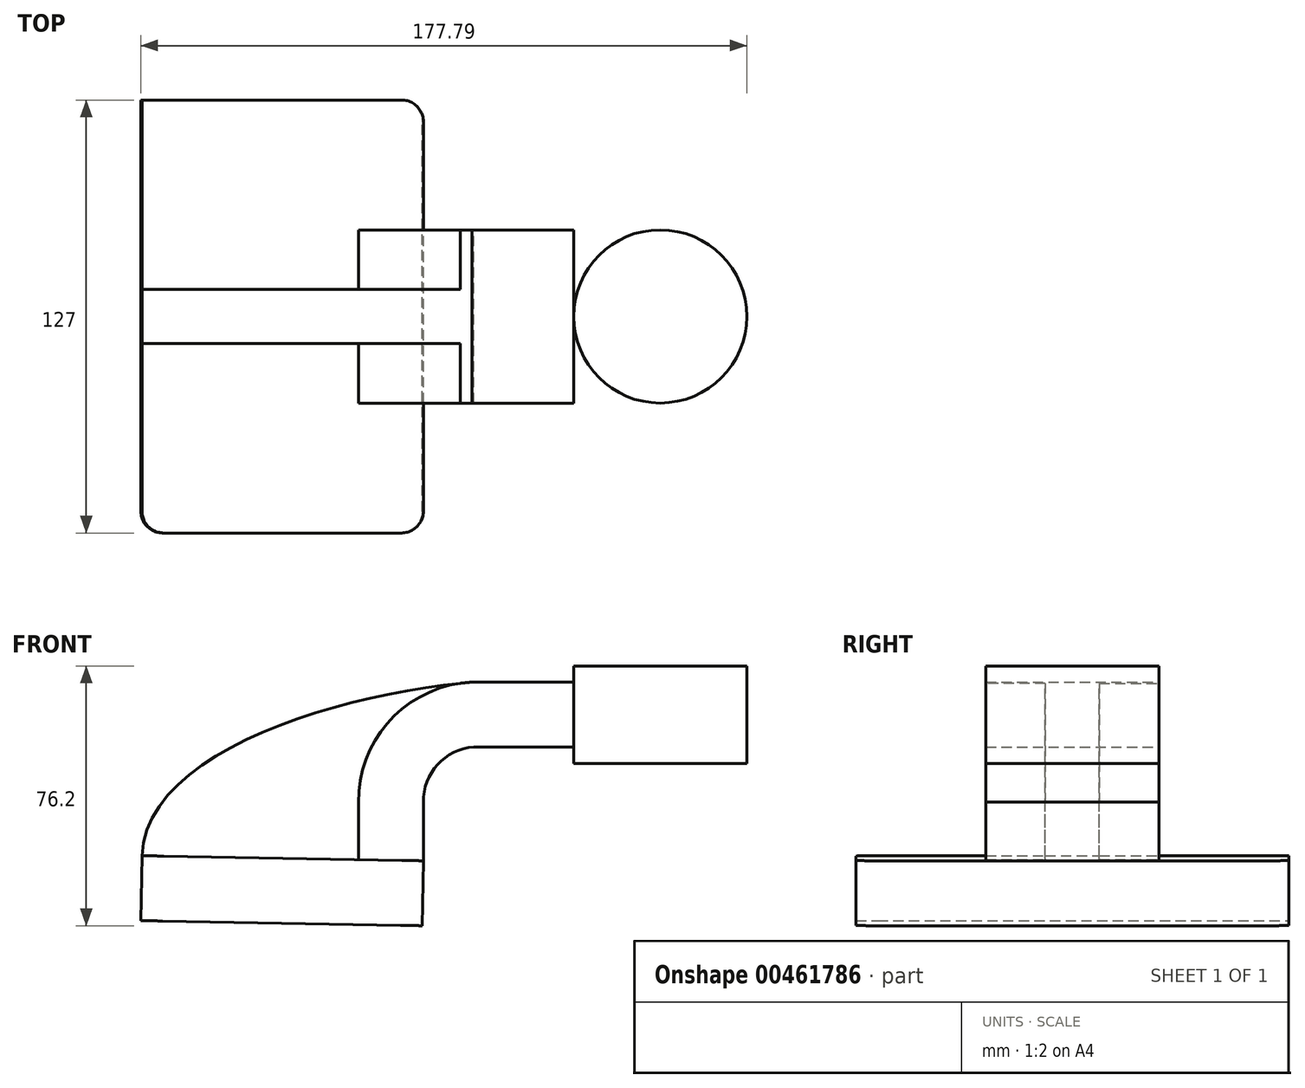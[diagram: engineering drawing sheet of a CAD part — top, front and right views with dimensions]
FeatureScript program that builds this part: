
annotation { "Feature Type Name" : "Feature", "Feature Type Description" : "" }
export const myFeature = defineFeature(function(context is Context, id is Id, definition is map)
    precondition{}
    {
        {
            var Q0;
            Q0=qCreatedBy(makeId("Front.planeOp"),FACE);
            var sketch = newSketch(context, id + "F0", { "sketchPlane" : qUnion([Q0])});
            skLineSegment(sketch, "E0.bottom", {"start": v(41.1, -10.27) * mm, "end": v(-41.44, -8.77) * mm});
            skLineSegment(sketch, "E0.top", {"start": v(41.44, 8.77) * mm, "end": v(-41.1, 10.27) * mm});
            skLineSegment(sketch, "E0.left", {"start": v(41.1, -10.27) * mm, "end": v(41.44, 8.77) * mm});
            skLineSegment(sketch, "E0.right", {"start": v(-41.44, -8.77) * mm, "end": v(-41.1, 10.27) * mm});
            skPoint(sketch, "E0.middle", {"position": v(0, 0) * mm});
            skLineSegment(sketch, "E1", {"start": v(41.44, 8.77) * mm, "end": v(41.45, 26.02) * mm});
            skLineSegment(sketch, "E2.bottom", {"start": v(110.95, 37.35) * mm, "end": v(60.15, 37.35) * mm});
            skLineSegment(sketch, "E2.top", {"start": v(110.95, 65.93) * mm, "end": v(60.15, 65.93) * mm});
            skLineSegment(sketch, "E2.left", {"start": v(110.95, 37.35) * mm, "end": v(110.95, 65.93) * mm});
            skLineSegment(sketch, "E2.right", {"start": v(60.15, 37.35) * mm, "end": v(60.15, 65.93) * mm});
            skPoint(sketch, "E2.middle", {"position": v(85.55, 51.64) * mm});
            skArc(sketch, "E3", {"start": v(56.2, 42.13) * mm, "mid": v(45.62, 37) * mm, "end": v(41.45, 26.02) * mm});
            skLineSegment(sketch, "E4", {"start": v(56.2, 42.13) * mm, "end": v(85.55, 42.13) * mm});
            skLineSegment(sketch, "E5.0", {"start": v(55.64, 61.18) * mm, "end": v(85.55, 61.18) * mm});
            skArc(sketch, "E5.1", {"start": v(55.64, 61.18) * mm, "mid": v(31.9, 50.24) * mm, "end": v(22.4, 25.9) * mm});
            skLineSegment(sketch, "E5.2", {"start": v(22.4, 9.37) * mm, "end": v(22.4, 25.9) * mm});
            skLineSegment(sketch, "E6", {"start": v(85.55, 65.93) * mm, "end": v(85.55, 37.35) * mm});
            skFitSpline(sketch, "E7", {"points": [v(-41.1, 10.27) * mm, v(55.64, 61.18) * mm], "startDerivative": vector(3.4, 93.06) * mm, "endDerivative": vector(113.48, 10) * mm});
            skLineSegment(sketch, "E8", {"start": v(22.4, 9.37) * mm, "end": v(22.4, 9.12) * mm});
            skSolve(sketch);
        }
        {
            var Q0;
            Q0=makeQuery(id+"F0.imprint","IMPRINT",FACE,{"disambiguationData":[TD([[makeQuery(id+"F0.imprint","IMPRINT",EDGE,{"derivedFrom":sQuery(id+"F0.wireOp",EDGE,"E0.bottom")}),-1.0]])]});
            extrude(context, id + "F1", {"entities" : qUnion([Q0]), "endBound" : BoundingType.SYMMETRIC, "depth" : 127 * mm});
        }
        {
            var Q0;
            {var subQ0=sQuery(id+"F0.wireOp",EDGE,"E4");var subQ1=sQuery(id+"F0.wireOp",EDGE,"E2.right");var subQ2=makeQuery(id+"F0.imprint","INTERSECT",VERTEX,{"derivedFrom":[subQ1,subQ0]});Q0=makeQuery(id+"F0.imprint","IMPRINT",FACE,{"disambiguationData":[TD([[makeQuery(id+"F0.imprint","IMPRINT",EDGE,{"disambiguationData":[TD([[subQ2,-1.0]])],"derivedFrom":subQ1}),-1.0]])]});}
            var Q1;
            {var subQ6=sQuery(id+"F0.wireOp",EDGE,"E1");Q1=makeQuery(id+"F0.imprint","IMPRINT",FACE,{"disambiguationData":[TD([[makeQuery(id+"F0.imprint","IMPRINT",EDGE,{"derivedFrom":subQ6}),1.0]])]});}
            extrude(context, id + "F2", {"entities" : qUnion([Q0, Q1]), "operationType" : NewBodyOperationType.ADD, "endBound" : BoundingType.SYMMETRIC, "depth" : 50.8 * mm});
        }
        {
            var Q0;
            {var subQ0=sQuery(id+"F0.wireOp",EDGE,"E5.2");Q0=makeQuery(id+"F0.imprint","IMPRINT",FACE,{"disambiguationData":[TD([[makeQuery(id+"F0.imprint","IMPRINT",EDGE,{"derivedFrom":subQ0}),1.0]])]});}
            extrude(context, id + "F3", {"entities" : qUnion([Q0]), "operationType" : NewBodyOperationType.ADD, "endBound" : BoundingType.SYMMETRIC, "depth" : 15.88 * mm});
        }
        {
            var Q0;
            {var subQ4=sQuery(id+"F0.wireOp",EDGE,"E2.left");Q0=makeQuery(id+"F0.imprint","IMPRINT",FACE,{"disambiguationData":[TD([[makeQuery(id+"F0.imprint","IMPRINT",EDGE,{"derivedFrom":subQ4}),1.0]])]});}
            var Q1;
            Q1=sQuery(id+"F0.wireOp",EDGE,"E2.left");
            revolve(context, id + "F4", {"operationType" : NewBodyOperationType.ADD, "entities" : qUnion([Q0]), "axis" : qUnion([Q1]), "revolveType" : RevolveType.FULL});
        }
        {
            var Q0;
            Q0=makeQuery(id+"F1.opExtrude","CAP_EDGE",EDGE,{"disambiguationData":[OSD([sQuery(id+"F0.wireOp",EDGE,"E0.left")])],"isStart":false});
            var Q1;
            Q1=makeQuery(id+"F1.opExtrude","CAP_EDGE",EDGE,{"disambiguationData":[OSD([sQuery(id+"F0.wireOp",EDGE,"E0.right")])],"isStart":false});
            var Q2;
            Q2=makeQuery(id+"F1.opExtrude","CAP_EDGE",EDGE,{"disambiguationData":[OSD([sQuery(id+"F0.wireOp",EDGE,"E0.left")])],"isStart":true});
            fillet(context, id + "F5", {"entities" : qUnion([Q0, Q1, Q2]), "radius" : 6.35 * mm, "tangentPropagation" : true, "allowEdgeOverflow" : false});
        }
    });
